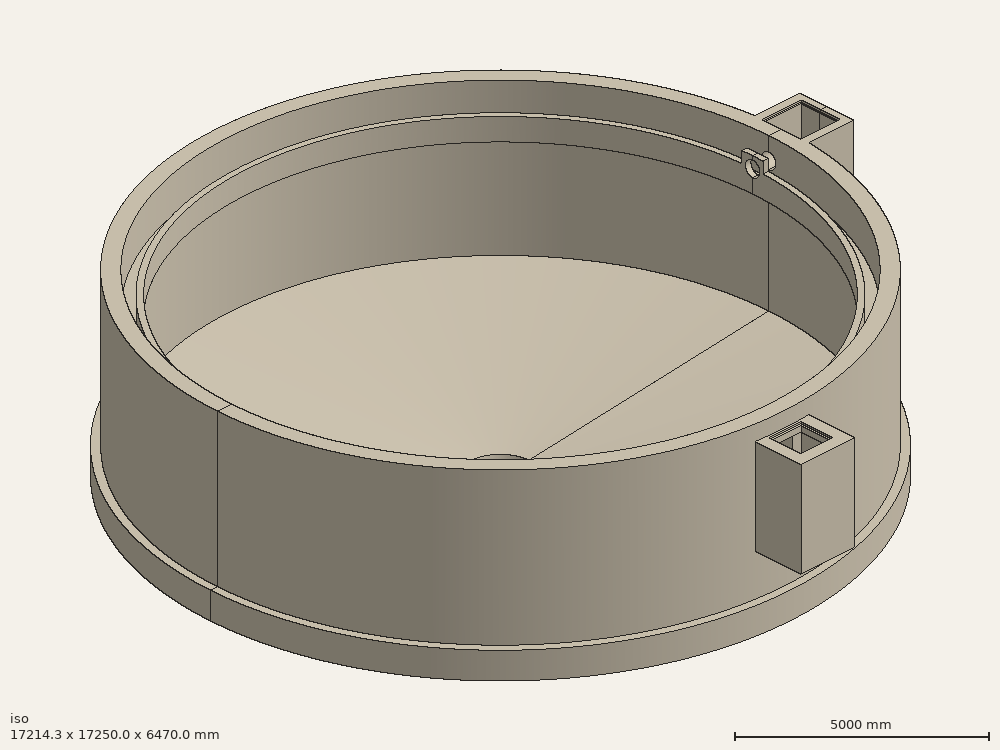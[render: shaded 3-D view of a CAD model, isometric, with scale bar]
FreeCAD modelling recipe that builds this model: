
FCSTD DOCUMENT  (FreeCAD 1.0R39109 (Git))
Label: body15.0m
License: All rights reserved
LicenseURL: https://en.wikipedia.org/wiki/All_rights_reserved
objects: Part::Feature×3, Part::FeaturePython×3, Part::MultiFuse×1, Part::Part2DObjectPython×1, App::DocumentObjectGroup×1, App::Part×1
note: 8 computed .brp shape members not serialized (recipe doc carries the construction recipe); baked Part::Feature solids carry a one-line shape summary decoded from their .brp

FEATURE [Part::Feature] Part__Feature  label="\X2\7D426C888EAF4F5353F3\X0\_1400 v8"
  shape: bbox 17210 x 17250 x 6470 mm, 65 faces (baked)
FEATURE [Part::Feature] Part__Feature001  label="\X2\7D426C888EAF4F5353F3\X0\_1400 v009"
  shape: bbox 1000 x 1000 x 230 mm, 5 faces (baked)
FEATURE [Part::Feature] Part__Feature002  label="\X2\7D426C888EAF4F5353F3\X0\_1400 v010"
  shape: bbox 1000 x 1000 x 230 mm, 5 faces (baked)
FEATURE [Part::MultiFuse] Fusion
  Refine = true
  Shapes = -> [Part__Feature,Part__Feature001,Part__Feature002]
FEATURE [Part::Part2DObjectPython] Rectangle  # Draft 2D object (typed FeaturePython)
  Area = 1.55372e+08
  ChamferSize = 0
  Columns = 1
  FilletRadius = 0
  Height = 8068.38
  Length = 19256.9
  MakeFace = true
  Placement = pos=(-9184.37,3.136e-13,-1420.94) rot=(1,0,0;1.5708rad)
  Rows = 1
FEATURE [Part::FeaturePython] Slice  # WARN: FeaturePython — macro-defined, semantics opaque (R4)
  Base = -> Fusion
  Mode = 1
  Tolerance = 0
  Tools = -> [Rectangle]
FEATURE [Part::FeaturePython] Slice_child0  label="Slice.0"  # WARN: FeaturePython — macro-defined, semantics opaque (R4)
  Base = -> Slice
  FilterType = 1
  Invert = false
  OverrideMaxVal = 0
  WindowFrom = 80
  WindowTo = 100
  items = 0
FEATURE [Part::FeaturePython] Slice_child1  label="Slice.1"  # WARN: FeaturePython — macro-defined, semantics opaque (R4)
  Base = -> Slice
  FilterType = 1
  Invert = false
  OverrideMaxVal = 0
  WindowFrom = 80
  WindowTo = 100
  items = 1
FEATURE [App::DocumentObjectGroup] GrExplode_Slice  label="Exploded Slice"
  Group = -> [Slice_child0,Slice_child1]
FEATURE [App::Part] _X2_7D426C888EAF4F5353F3_X0__1400_v8  label="body15.0m"
  Group = -> [Part__Feature,Part__Feature002,Part__Feature001,Fusion,Rectangle,Slice,Slice_child0,Slice_child1,GrExplode_Slice]
  Origin = -> Origin
